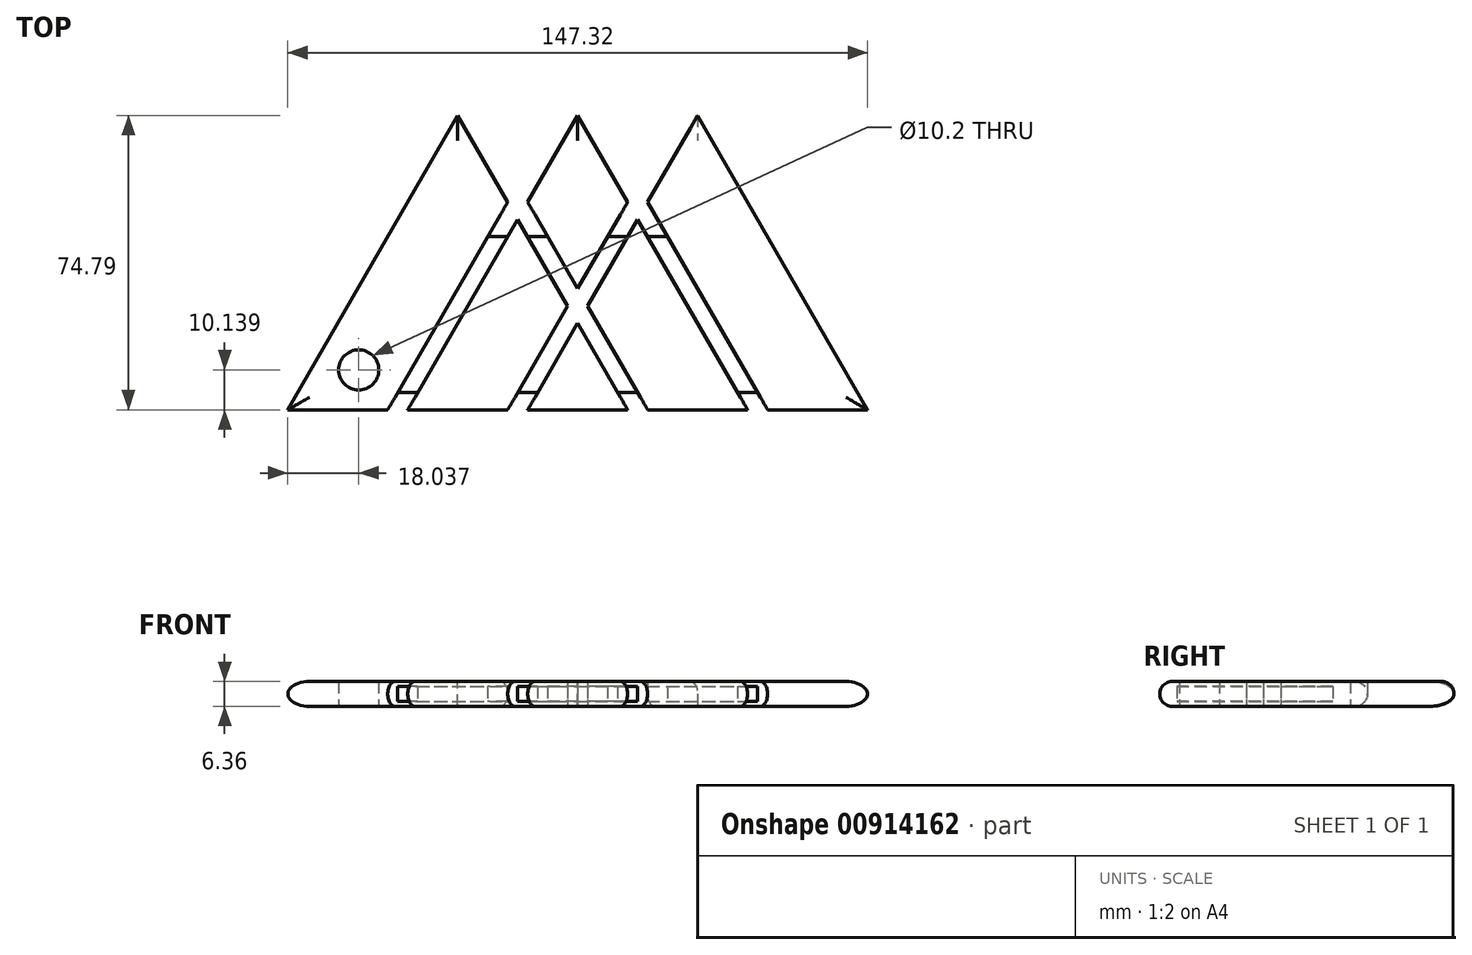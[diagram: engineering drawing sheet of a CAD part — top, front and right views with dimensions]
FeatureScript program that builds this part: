
annotation { "Feature Type Name" : "Feature", "Feature Type Description" : "" }
export const myFeature = defineFeature(function(context is Context, id is Id, definition is map)
    precondition{}
    {
        {
            var Q0;
            Q0=qCreatedBy(makeId("Top.planeOp"),FACE);
            var sketch = newSketch(context, id + "F0", { "sketchPlane" : qUnion([Q0])});
            skLineSegment(sketch, "E0", {"start": v(0, 0) * mm, "end": v(25.4, 0) * mm});
            skLineSegment(sketch, "E1", {"start": v(30.48, 0) * mm, "end": v(55.88, 0) * mm});
            skLineSegment(sketch, "E2", {"start": v(60.96, 0) * mm, "end": v(86.36, 0) * mm});
            skLineSegment(sketch, "E3", {"start": v(91.44, 0) * mm, "end": v(116.84, 0) * mm});
            skLineSegment(sketch, "E4", {"start": v(121.92, 0) * mm, "end": v(147.32, 0) * mm});
            skLineSegment(sketch, "E5", {"start": v(60.96, 0) * mm, "end": v(73.66, 22) * mm});
            skPoint(sketch, "E5.endSnap0", {"position": v(73.66, 0) * mm});
            skLineSegment(sketch, "E6", {"start": v(73.66, 22) * mm, "end": v(86.36, 0) * mm});
            skLineSegment(sketch, "E7", {"start": v(91.44, 0) * mm, "end": v(76.2, 26.4) * mm});
            skLineSegment(sketch, "E8", {"start": v(88.9, 48.4) * mm, "end": v(116.84, 0) * mm});
            skLineSegment(sketch, "E9", {"start": v(88.9, 48.4) * mm, "end": v(76.2, 26.4) * mm});
            skLineSegment(sketch, "E10", {"start": v(91.44, 52.8) * mm, "end": v(121.92, 0) * mm});
            skLineSegment(sketch, "E11", {"start": v(91.44, 52.8) * mm, "end": v(104.14, 74.79) * mm});
            skLineSegment(sketch, "E12", {"start": v(104.14, 74.79) * mm, "end": v(147.32, 0) * mm});
            skLineSegment(sketch, "E13", {"start": v(55.88, 0) * mm, "end": v(71.12, 26.4) * mm});
            skLineSegment(sketch, "E14", {"start": v(30.48, 0) * mm, "end": v(58.42, 48.4) * mm});
            skLineSegment(sketch, "E15", {"start": v(25.4, 0) * mm, "end": v(55.88, 52.8) * mm});
            skLineSegment(sketch, "E16", {"start": v(0, 0) * mm, "end": v(43.18, 74.79) * mm});
            skLineSegment(sketch, "E17", {"start": v(73.66, 30.8) * mm, "end": v(86.36, 52.8) * mm});
            skLineSegment(sketch, "E18", {"start": v(73.66, 30.8) * mm, "end": v(60.96, 52.8) * mm});
            skLineSegment(sketch, "E19", {"start": v(86.36, 52.8) * mm, "end": v(73.66, 74.79) * mm});
            skLineSegment(sketch, "E20", {"start": v(60.96, 52.8) * mm, "end": v(73.66, 74.79) * mm});
            skLineSegment(sketch, "E21", {"start": v(43.18, 74.79) * mm, "end": v(55.88, 52.8) * mm});
            skLineSegment(sketch, "E22", {"start": v(58.42, 48.4) * mm, "end": v(71.12, 26.4) * mm});
            skLineSegment(sketch, "E23", {"start": v(116.84, 0) * mm, "end": v(114.3, 4.4) * mm});
            skLineSegment(sketch, "E24", {"start": v(114.3, 4.4) * mm, "end": v(119.38, 4.4) * mm});
            skLineSegment(sketch, "E25", {"start": v(86.36, 0) * mm, "end": v(83.82, 4.4) * mm});
            skLineSegment(sketch, "E26", {"start": v(83.82, 4.4) * mm, "end": v(88.9, 4.4) * mm});
            skLineSegment(sketch, "E27", {"start": v(60.96, 0) * mm, "end": v(63.5, 4.4) * mm});
            skLineSegment(sketch, "E28", {"start": v(63.5, 4.4) * mm, "end": v(58.42, 4.4) * mm});
            skLineSegment(sketch, "E29", {"start": v(30.48, 0) * mm, "end": v(33.02, 4.4) * mm});
            skLineSegment(sketch, "E30", {"start": v(33.02, 4.4) * mm, "end": v(27.94, 4.4) * mm});
            skLineSegment(sketch, "E31", {"start": v(88.9, 48.4) * mm, "end": v(91.44, 44) * mm});
            skLineSegment(sketch, "E32", {"start": v(91.44, 44) * mm, "end": v(96.52, 44) * mm});
            skLineSegment(sketch, "E33", {"start": v(88.9, 48.4) * mm, "end": v(86.36, 44) * mm});
            skLineSegment(sketch, "E34", {"start": v(86.36, 44) * mm, "end": v(81.28, 44) * mm});
            skLineSegment(sketch, "E35", {"start": v(58.42, 48.4) * mm, "end": v(60.96, 44) * mm});
            skLineSegment(sketch, "E36", {"start": v(60.96, 44) * mm, "end": v(66.04, 44) * mm});
            skLineSegment(sketch, "E37", {"start": v(58.42, 48.4) * mm, "end": v(55.88, 44) * mm});
            skLineSegment(sketch, "E38", {"start": v(55.88, 44) * mm, "end": v(50.8, 44) * mm});
            skCircle(sketch, "E39", {"center": v(18.04, 10.14) * mm, "radius": 5.1 * mm});
            skSolve(sketch);
        }
        {
            var Q0;
            {var subQ3=sQuery(id+"F0.wireOp",EDGE,"E1");Q0=makeQuery(id+"F0.imprint","IMPRINT",FACE,{"disambiguationData":[TD([[makeQuery(id+"F0.imprint","IMPRINT",EDGE,{"derivedFrom":subQ3}),1.0]])]});}
            var Q1;
            {var subQ1=sQuery(id+"F0.wireOp",EDGE,"E19");Q1=makeQuery(id+"F0.imprint","IMPRINT",FACE,{"disambiguationData":[TD([[makeQuery(id+"F0.imprint","IMPRINT",EDGE,{"derivedFrom":subQ1}),1.0]])]});}
            var Q2;
            {var subQ3=sQuery(id+"F0.wireOp",EDGE,"E3");Q2=makeQuery(id+"F0.imprint","IMPRINT",FACE,{"disambiguationData":[TD([[makeQuery(id+"F0.imprint","IMPRINT",EDGE,{"derivedFrom":subQ3}),1.0]])]});}
            var Q3;
            Q3=makeQuery(id+"F0.imprint","IMPRINT",FACE,{"disambiguationData":[TD([[makeQuery(id+"F0.imprint","IMPRINT",EDGE,{"derivedFrom":sQuery(id+"F0.wireOp",EDGE,"E2")}),1.0]])]});
            var Q4;
            {var subQ3=sQuery(id+"F0.wireOp",EDGE,"E4");Q4=makeQuery(id+"F0.imprint","IMPRINT",FACE,{"disambiguationData":[TD([[makeQuery(id+"F0.imprint","IMPRINT",EDGE,{"derivedFrom":subQ3}),1.0]])]});}
            var Q5;
            {var subQ3=sQuery(id+"F0.wireOp",EDGE,"E0");Q5=makeQuery(id+"F0.imprint","IMPRINT",FACE,{"disambiguationData":[TD([[makeQuery(id+"F0.imprint","IMPRINT",EDGE,{"derivedFrom":subQ3}),1.0]])]});}
            extrude(context, id + "F1", {"entities" : qUnion([Q0, Q1, Q2, Q3, Q4, Q5]), "endBound" : BoundingType.SYMMETRIC, "offsetDistance" : 25.4 * mm, "depth" : 6.35 * mm});
        }
        {
            var Q0;
            Q0=makeQuery(id+"F0.imprint","IMPRINT",FACE,{"disambiguationData":[TD([[makeQuery(id+"F0.imprint","IMPRINT",EDGE,{"derivedFrom":sQuery(id+"F0.wireOp",EDGE,"E8")}),1.0]])]});
            var Q1;
            Q1=makeQuery(id+"F0.imprint","IMPRINT",FACE,{"disambiguationData":[TD([[makeQuery(id+"F0.imprint","IMPRINT",EDGE,{"derivedFrom":sQuery(id+"F0.wireOp",EDGE,"E5")}),1.0]])]});
            var Q2;
            Q2=makeQuery(id+"F0.imprint","IMPRINT",FACE,{"disambiguationData":[TD([[makeQuery(id+"F0.imprint","IMPRINT",EDGE,{"derivedFrom":sQuery(id+"F0.wireOp",EDGE,"E14")}),1.0]])]});
            extrude(context, id + "F2", {"entities" : qUnion([Q0, Q1, Q2]), "endBound" : BoundingType.SYMMETRIC, "depth" : 3.8 * mm});
        }
        {
            var Q0;
            Q0=makeQuery(id+"F1.opExtrude","CAP_EDGE",EDGE,{"disambiguationData":[OSD([sQuery(id+"F0.wireOp",EDGE,"E16")])],"isStart":false});
            var Q1;
            Q1=makeQuery(id+"F1.opExtrude","CAP_EDGE",EDGE,{"disambiguationData":[OSD([sQuery(id+"F0.wireOp",EDGE,"E16")])],"isStart":true});
            var Q2;
            Q2=makeQuery(id+"F1.opExtrude","CAP_EDGE",EDGE,{"disambiguationData":[OSD([sQuery(id+"F0.wireOp",EDGE,"E20")])],"isStart":false});
            var Q3;
            Q3=makeQuery(id+"F1.opExtrude","CAP_EDGE",EDGE,{"disambiguationData":[OSD([sQuery(id+"F0.wireOp",EDGE,"E19")])],"isStart":false});
            var Q4;
            Q4=makeQuery(id+"F1.opExtrude","CAP_EDGE",EDGE,{"disambiguationData":[OSD([sQuery(id+"F0.wireOp",EDGE,"E19")])],"isStart":true});
            var Q5;
            Q5=makeQuery(id+"F1.opExtrude","CAP_EDGE",EDGE,{"disambiguationData":[OSD([sQuery(id+"F0.wireOp",EDGE,"E20")])],"isStart":true});
            var Q6;
            Q6=makeQuery(id+"F1.opExtrude","CAP_EDGE",EDGE,{"disambiguationData":[OSD([sQuery(id+"F0.wireOp",EDGE,"E0")])],"isStart":true});
            var Q7;
            Q7=makeQuery(id+"F1.opExtrude","CAP_EDGE",EDGE,{"disambiguationData":[OSD([sQuery(id+"F0.wireOp",EDGE,"E1")])],"isStart":true});
            var Q8;
            Q8=makeQuery(id+"F1.opExtrude","CAP_EDGE",EDGE,{"disambiguationData":[OSD([sQuery(id+"F0.wireOp",EDGE,"E2")])],"isStart":true});
            var Q9;
            Q9=makeQuery(id+"F1.opExtrude","CAP_EDGE",EDGE,{"disambiguationData":[OSD([sQuery(id+"F0.wireOp",EDGE,"E3")])],"isStart":true});
            var Q10;
            Q10=makeQuery(id+"F1.opExtrude","CAP_EDGE",EDGE,{"disambiguationData":[OSD([sQuery(id+"F0.wireOp",EDGE,"E4")])],"isStart":true});
            var Q11;
            Q11=makeQuery(id+"F1.opExtrude","CAP_EDGE",EDGE,{"disambiguationData":[OSD([sQuery(id+"F0.wireOp",EDGE,"E12")])],"isStart":true});
            var Q12;
            Q12=makeQuery(id+"F1.opExtrude","CAP_EDGE",EDGE,{"disambiguationData":[OSD([sQuery(id+"F0.wireOp",EDGE,"E11")])],"isStart":true});
            var Q13;
            Q13=makeQuery(id+"F1.opExtrude","CAP_EDGE",EDGE,{"disambiguationData":[OSD([sQuery(id+"F0.wireOp",EDGE,"E0")])],"isStart":false});
            var Q14;
            Q14=makeQuery(id+"F1.opExtrude","CAP_EDGE",EDGE,{"disambiguationData":[OSD([sQuery(id+"F0.wireOp",EDGE,"E1")])],"isStart":false});
            var Q15;
            Q15=makeQuery(id+"F1.opExtrude","CAP_EDGE",EDGE,{"disambiguationData":[OSD([sQuery(id+"F0.wireOp",EDGE,"E2")])],"isStart":false});
            var Q16;
            Q16=makeQuery(id+"F1.opExtrude","CAP_EDGE",EDGE,{"disambiguationData":[OSD([sQuery(id+"F0.wireOp",EDGE,"E3")])],"isStart":false});
            var Q17;
            Q17=makeQuery(id+"F1.opExtrude","CAP_EDGE",EDGE,{"disambiguationData":[OSD([sQuery(id+"F0.wireOp",EDGE,"E4")])],"isStart":false});
            var Q18;
            Q18=makeQuery(id+"F1.opExtrude","CAP_EDGE",EDGE,{"disambiguationData":[OSD([sQuery(id+"F0.wireOp",EDGE,"E12")])],"isStart":false});
            var Q19;
            Q19=makeQuery(id+"F1.opExtrude","CAP_EDGE",EDGE,{"disambiguationData":[OSD([sQuery(id+"F0.wireOp",EDGE,"E21")])],"isStart":false});
            var Q20;
            Q20=makeQuery(id+"F1.opExtrude","CAP_EDGE",EDGE,{"disambiguationData":[OSD([sQuery(id+"F0.wireOp",EDGE,"E21")])],"isStart":true});
            fillet(context, id + "F3", {"entities" : qUnion([Q0, Q1, Q2, Q3, Q4, Q5, Q6, Q7, Q8, Q9, Q10, Q11, Q12, Q13, Q14, Q15, Q16, Q17, Q18, Q19, Q20]), "radius" : 3.17 * mm, "tangentPropagation" : true, "allowEdgeOverflow" : false});
        }
    });
